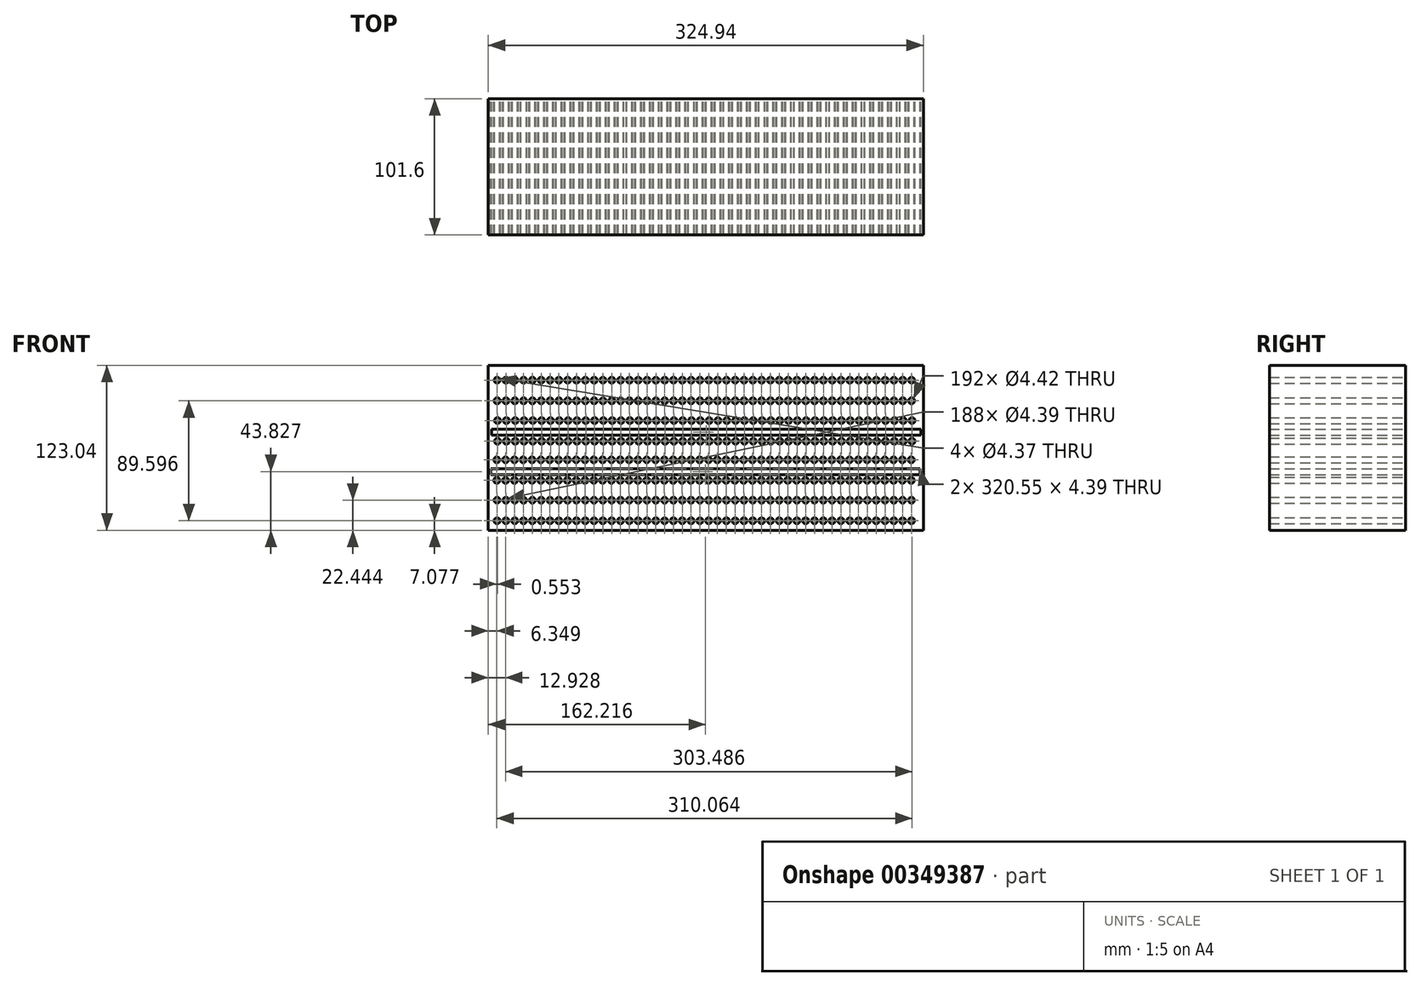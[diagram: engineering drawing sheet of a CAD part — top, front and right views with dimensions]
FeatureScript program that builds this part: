
annotation { "Feature Type Name" : "Feature", "Feature Type Description" : "" }
export const myFeature = defineFeature(function(context is Context, id is Id, definition is map)
    precondition{}
    {
        {
            var Q0;
            Q0=qCreatedBy(makeId("Front.planeOp"),FACE);
            var sketch = newSketch(context, id + "F0", { "sketchPlane" : qUnion([Q0])});
            skLineSegment(sketch, "E0.bottom", {"start": v(-162.47, -61.52) * mm, "end": v(162.47, -61.52) * mm});
            skLineSegment(sketch, "E0.top", {"start": v(-162.47, 61.52) * mm, "end": v(162.47, 61.52) * mm});
            skLineSegment(sketch, "E0.left", {"start": v(-162.47, -61.52) * mm, "end": v(-162.47, 61.52) * mm});
            skLineSegment(sketch, "E0.right", {"start": v(162.47, -61.52) * mm, "end": v(162.47, 61.52) * mm});
            skPoint(sketch, "E0.middle", {"position": v(0, 0) * mm});
            skLineSegment(sketch, "E1.left", {"start": v(-162.47, 61.52) * mm, "end": v(-162.47, 59.3) * mm});
            skLineSegment(sketch, "E1.right", {"start": v(162.47, 61.52) * mm, "end": v(162.47, 59.3) * mm});
            skLineSegment(sketch, "E2.top", {"start": v(-162.47, -61.52) * mm, "end": v(-160.27, -61.52) * mm});
            skLineSegment(sketch, "E2.left", {"start": v(-162.47, 59.3) * mm, "end": v(-162.47, -61.52) * mm});
            skLineSegment(sketch, "E3.top", {"start": v(162.47, -61.52) * mm, "end": v(160.27, -61.52) * mm});
            skLineSegment(sketch, "E3.left", {"start": v(162.47, 59.3) * mm, "end": v(162.47, -61.52) * mm});
            skLineSegment(sketch, "E4.bottom", {"start": v(-160.27, -61.52) * mm, "end": v(160.27, -61.52) * mm});
            skLineSegment(sketch, "E5.bottom", {"start": v(-160.27, 59.3) * mm, "end": v(160.27, 59.3) * mm});
            skLineSegment(sketch, "E5.top", {"start": v(-160.27, 54.91) * mm, "end": v(160.27, 54.91) * mm});
            skLineSegment(sketch, "E5.left", {"start": v(-160.27, 59.3) * mm, "end": v(-160.27, 54.91) * mm});
            skLineSegment(sketch, "E5.right", {"start": v(160.27, 59.3) * mm, "end": v(160.27, 54.91) * mm});
            skLineSegment(sketch, "E6.bottom", {"start": v(-160.27, 54.91) * mm, "end": v(-158.08, 54.91) * mm});
            skLineSegment(sketch, "E7.bottom", {"start": v(160.27, 54.91) * mm, "end": v(158.08, 54.91) * mm});
            skCircle(sketch, "E8", {"center": v(-155.87, 50.52) * mm, "radius": 2.18 * mm});
            skCircle(sketch, "E9", {"center": v(-149.29, 50.52) * mm, "radius": 2.2 * mm});
            skCircle(sketch, "E10", {"center": v(-142.68, 50.52) * mm, "radius": 2.2 * mm});
            skCircle(sketch, "E11", {"center": v(-136.1, 50.52) * mm, "radius": 2.2 * mm});
            skCircle(sketch, "E12", {"center": v(-129.51, 50.52) * mm, "radius": 2.2 * mm});
            skCircle(sketch, "E13", {"center": v(-122.94, 50.52) * mm, "radius": 2.2 * mm});
            skCircle(sketch, "E14", {"center": v(-116.34, 50.52) * mm, "radius": 2.2 * mm});
            skCircle(sketch, "E15", {"center": v(-109.77, 50.52) * mm, "radius": 2.2 * mm});
            skCircle(sketch, "E16", {"center": v(-103.17, 50.52) * mm, "radius": 2.2 * mm});
            skCircle(sketch, "E17", {"center": v(-96.6, 50.52) * mm, "radius": 2.2 * mm});
            skCircle(sketch, "E18", {"center": v(-90, 50.52) * mm, "radius": 2.2 * mm});
            skCircle(sketch, "E19", {"center": v(-83.43, 50.52) * mm, "radius": 2.2 * mm});
            skCircle(sketch, "E20", {"center": v(-76.84, 50.52) * mm, "radius": 2.2 * mm});
            skCircle(sketch, "E21", {"center": v(-70.26, 50.52) * mm, "radius": 2.2 * mm});
            skCircle(sketch, "E22", {"center": v(-63.67, 50.52) * mm, "radius": 2.2 * mm});
            skCircle(sketch, "E23", {"center": v(-57.09, 50.52) * mm, "radius": 2.2 * mm});
            skCircle(sketch, "E24", {"center": v(-50.5, 50.52) * mm, "radius": 2.2 * mm});
            skCircle(sketch, "E25", {"center": v(-43.92, 50.52) * mm, "radius": 2.2 * mm});
            skCircle(sketch, "E26", {"center": v(-37.33, 50.52) * mm, "radius": 2.2 * mm});
            skCircle(sketch, "E27", {"center": v(-30.75, 50.52) * mm, "radius": 2.2 * mm});
            skCircle(sketch, "E28", {"center": v(-24.16, 50.52) * mm, "radius": 2.2 * mm});
            skCircle(sketch, "E29", {"center": v(-17.58, 50.52) * mm, "radius": 2.2 * mm});
            skCircle(sketch, "E30", {"center": v(-10.99, 50.52) * mm, "radius": 2.2 * mm});
            skCircle(sketch, "E31", {"center": v(-4.4, 50.52) * mm, "radius": 2.2 * mm});
            skCircle(sketch, "E32", {"center": v(2.18, 50.52) * mm, "radius": 2.2 * mm});
            skCircle(sketch, "E33", {"center": v(8.76, 50.52) * mm, "radius": 2.2 * mm});
            skCircle(sketch, "E34", {"center": v(15.35, 50.52) * mm, "radius": 2.2 * mm});
            skCircle(sketch, "E35", {"center": v(21.93, 50.52) * mm, "radius": 2.2 * mm});
            skCircle(sketch, "E36", {"center": v(28.52, 50.52) * mm, "radius": 2.2 * mm});
            skCircle(sketch, "E37", {"center": v(35.1, 50.52) * mm, "radius": 2.2 * mm});
            skCircle(sketch, "E38", {"center": v(41.7, 50.52) * mm, "radius": 2.2 * mm});
            skCircle(sketch, "E39", {"center": v(48.27, 50.52) * mm, "radius": 2.2 * mm});
            skCircle(sketch, "E40", {"center": v(54.86, 50.52) * mm, "radius": 2.2 * mm});
            skCircle(sketch, "E41", {"center": v(61.44, 50.52) * mm, "radius": 2.2 * mm});
            skCircle(sketch, "E42", {"center": v(68.03, 50.52) * mm, "radius": 2.2 * mm});
            skCircle(sketch, "E43", {"center": v(74.61, 50.52) * mm, "radius": 2.2 * mm});
            skCircle(sketch, "E44", {"center": v(81.2, 50.52) * mm, "radius": 2.2 * mm});
            skCircle(sketch, "E45", {"center": v(87.78, 50.52) * mm, "radius": 2.2 * mm});
            skCircle(sketch, "E46", {"center": v(94.37, 50.52) * mm, "radius": 2.2 * mm});
            skCircle(sketch, "E47", {"center": v(100.95, 50.52) * mm, "radius": 2.2 * mm});
            skCircle(sketch, "E48", {"center": v(107.54, 50.52) * mm, "radius": 2.2 * mm});
            skCircle(sketch, "E49", {"center": v(114.12, 50.52) * mm, "radius": 2.2 * mm});
            skCircle(sketch, "E50", {"center": v(120.71, 50.52) * mm, "radius": 2.2 * mm});
            skCircle(sketch, "E51", {"center": v(127.3, 50.52) * mm, "radius": 2.2 * mm});
            skCircle(sketch, "E52", {"center": v(133.9, 50.52) * mm, "radius": 2.2 * mm});
            skCircle(sketch, "E53", {"center": v(140.47, 50.52) * mm, "radius": 2.2 * mm});
            skCircle(sketch, "E54", {"center": v(147.07, 50.52) * mm, "radius": 2.2 * mm});
            skCircle(sketch, "E55", {"center": v(153.64, 50.52) * mm, "radius": 2.2 * mm});
            skLineSegment(sketch, "E56", {"start": v(-155.87, 43.94) * mm, "end": v(-158.08, 43.94) * mm});
            skLineSegment(sketch, "E57", {"start": v(-158.08, 43.94) * mm, "end": v(-160.27, 43.94) * mm});
            skLineSegment(sketch, "E58.bottom", {"start": v(-160.27, 43.94) * mm, "end": v(160.27, 43.94) * mm});
            skLineSegment(sketch, "E58.top", {"start": v(-160.27, 39.55) * mm, "end": v(160.27, 39.55) * mm});
            skLineSegment(sketch, "E58.left", {"start": v(-160.27, 43.94) * mm, "end": v(-160.27, 39.55) * mm});
            skLineSegment(sketch, "E58.right", {"start": v(160.27, 43.94) * mm, "end": v(160.27, 39.55) * mm});
            skCircle(sketch, "E59", {"center": v(-155.87, 35.15) * mm, "radius": 2.2 * mm});
            skCircle(sketch, "E60", {"center": v(-149.29, 35.15) * mm, "radius": 2.2 * mm});
            skCircle(sketch, "E61", {"center": v(-142.68, 35.15) * mm, "radius": 2.2 * mm});
            skCircle(sketch, "E62", {"center": v(-136.1, 35.15) * mm, "radius": 2.2 * mm});
            skCircle(sketch, "E63", {"center": v(-129.51, 35.15) * mm, "radius": 2.2 * mm});
            skCircle(sketch, "E64", {"center": v(-122.94, 35.15) * mm, "radius": 2.2 * mm});
            skCircle(sketch, "E65", {"center": v(-116.34, 35.15) * mm, "radius": 2.2 * mm});
            skCircle(sketch, "E66", {"center": v(-109.77, 35.15) * mm, "radius": 2.2 * mm});
            skCircle(sketch, "E67", {"center": v(-103.17, 35.15) * mm, "radius": 2.2 * mm});
            skCircle(sketch, "E68", {"center": v(-96.6, 35.15) * mm, "radius": 2.2 * mm});
            skCircle(sketch, "E69", {"center": v(-90, 35.15) * mm, "radius": 2.2 * mm});
            skCircle(sketch, "E70", {"center": v(-83.43, 35.15) * mm, "radius": 2.2 * mm});
            skCircle(sketch, "E71", {"center": v(-76.84, 35.15) * mm, "radius": 2.2 * mm});
            skCircle(sketch, "E72", {"center": v(-70.26, 35.15) * mm, "radius": 2.2 * mm});
            skCircle(sketch, "E73", {"center": v(-63.67, 35.15) * mm, "radius": 2.2 * mm});
            skCircle(sketch, "E74", {"center": v(-57.09, 35.15) * mm, "radius": 2.2 * mm});
            skCircle(sketch, "E75", {"center": v(-50.5, 35.15) * mm, "radius": 2.2 * mm});
            skCircle(sketch, "E76", {"center": v(-43.92, 35.15) * mm, "radius": 2.2 * mm});
            skCircle(sketch, "E77", {"center": v(-37.33, 35.15) * mm, "radius": 2.2 * mm});
            skCircle(sketch, "E78", {"center": v(-30.75, 35.15) * mm, "radius": 2.2 * mm});
            skCircle(sketch, "E79", {"center": v(-24.16, 35.15) * mm, "radius": 2.2 * mm});
            skCircle(sketch, "E80", {"center": v(-17.58, 35.15) * mm, "radius": 2.2 * mm});
            skCircle(sketch, "E81", {"center": v(-10.99, 35.15) * mm, "radius": 2.2 * mm});
            skCircle(sketch, "E82", {"center": v(-4.4, 35.15) * mm, "radius": 2.2 * mm});
            skCircle(sketch, "E83", {"center": v(2.18, 35.15) * mm, "radius": 2.2 * mm});
            skCircle(sketch, "E84", {"center": v(8.76, 35.15) * mm, "radius": 2.2 * mm});
            skCircle(sketch, "E85", {"center": v(15.35, 35.15) * mm, "radius": 2.2 * mm});
            skCircle(sketch, "E86", {"center": v(21.93, 35.15) * mm, "radius": 2.2 * mm});
            skCircle(sketch, "E87", {"center": v(28.52, 35.15) * mm, "radius": 2.2 * mm});
            skCircle(sketch, "E88", {"center": v(35.1, 35.15) * mm, "radius": 2.2 * mm});
            skCircle(sketch, "E89", {"center": v(41.7, 35.15) * mm, "radius": 2.2 * mm});
            skCircle(sketch, "E90", {"center": v(48.27, 35.15) * mm, "radius": 2.2 * mm});
            skCircle(sketch, "E91", {"center": v(54.86, 35.15) * mm, "radius": 2.2 * mm});
            skCircle(sketch, "E92", {"center": v(61.44, 35.15) * mm, "radius": 2.2 * mm});
            skCircle(sketch, "E93", {"center": v(68.03, 35.15) * mm, "radius": 2.2 * mm});
            skCircle(sketch, "E94", {"center": v(74.61, 35.15) * mm, "radius": 2.2 * mm});
            skCircle(sketch, "E95", {"center": v(81.2, 35.15) * mm, "radius": 2.2 * mm});
            skCircle(sketch, "E96", {"center": v(87.78, 35.15) * mm, "radius": 2.2 * mm});
            skCircle(sketch, "E97", {"center": v(94.37, 35.15) * mm, "radius": 2.2 * mm});
            skCircle(sketch, "E98", {"center": v(100.95, 35.15) * mm, "radius": 2.2 * mm});
            skCircle(sketch, "E99", {"center": v(107.54, 35.15) * mm, "radius": 2.2 * mm});
            skCircle(sketch, "E100", {"center": v(114.12, 35.15) * mm, "radius": 2.2 * mm});
            skCircle(sketch, "E101", {"center": v(120.71, 35.15) * mm, "radius": 2.2 * mm});
            skCircle(sketch, "E102", {"center": v(127.3, 35.15) * mm, "radius": 2.2 * mm});
            skCircle(sketch, "E103", {"center": v(133.9, 35.15) * mm, "radius": 2.2 * mm});
            skCircle(sketch, "E104", {"center": v(140.47, 35.15) * mm, "radius": 2.2 * mm});
            skCircle(sketch, "E105", {"center": v(147.07, 35.15) * mm, "radius": 2.2 * mm});
            skCircle(sketch, "E106", {"center": v(153.64, 35.15) * mm, "radius": 2.2 * mm});
            skLineSegment(sketch, "E107.bottom", {"start": v(-159.97, 29.14) * mm, "end": v(160.57, 29.14) * mm});
            skLineSegment(sketch, "E107.top", {"start": v(-159.97, 24.75) * mm, "end": v(160.57, 24.75) * mm});
            skLineSegment(sketch, "E108.bottom", {"start": v(-159.97, 24.75) * mm, "end": v(-157.78, 24.75) * mm});
            skLineSegment(sketch, "E109.bottom", {"start": v(160.57, 24.75) * mm, "end": v(158.38, 24.75) * mm});
            skCircle(sketch, "E110", {"center": v(-155.57, 20.35) * mm, "radius": 2.18 * mm});
            skCircle(sketch, "E111", {"center": v(-148.99, 20.35) * mm, "radius": 2.2 * mm});
            skCircle(sketch, "E112", {"center": v(-142.39, 20.35) * mm, "radius": 2.2 * mm});
            skCircle(sketch, "E113", {"center": v(-135.8, 20.35) * mm, "radius": 2.2 * mm});
            skCircle(sketch, "E114", {"center": v(-129.22, 20.35) * mm, "radius": 2.2 * mm});
            skCircle(sketch, "E115", {"center": v(-122.64, 20.35) * mm, "radius": 2.2 * mm});
            skCircle(sketch, "E116", {"center": v(-116.05, 20.35) * mm, "radius": 2.2 * mm});
            skCircle(sketch, "E117", {"center": v(-109.47, 20.35) * mm, "radius": 2.2 * mm});
            skCircle(sketch, "E118", {"center": v(-102.88, 20.35) * mm, "radius": 2.2 * mm});
            skCircle(sketch, "E119", {"center": v(-96.3, 20.35) * mm, "radius": 2.2 * mm});
            skCircle(sketch, "E120", {"center": v(-89.7, 20.35) * mm, "radius": 2.2 * mm});
            skCircle(sketch, "E121", {"center": v(-83.13, 20.35) * mm, "radius": 2.2 * mm});
            skCircle(sketch, "E122", {"center": v(-76.54, 20.35) * mm, "radius": 2.2 * mm});
            skCircle(sketch, "E123", {"center": v(-69.96, 20.35) * mm, "radius": 2.2 * mm});
            skCircle(sketch, "E124", {"center": v(-63.37, 20.35) * mm, "radius": 2.2 * mm});
            skCircle(sketch, "E125", {"center": v(-56.79, 20.35) * mm, "radius": 2.2 * mm});
            skCircle(sketch, "E126", {"center": v(-50.2, 20.35) * mm, "radius": 2.2 * mm});
            skCircle(sketch, "E127", {"center": v(-43.62, 20.35) * mm, "radius": 2.2 * mm});
            skCircle(sketch, "E128", {"center": v(-37.03, 20.35) * mm, "radius": 2.2 * mm});
            skCircle(sketch, "E129", {"center": v(-30.45, 20.35) * mm, "radius": 2.2 * mm});
            skCircle(sketch, "E130", {"center": v(-23.86, 20.35) * mm, "radius": 2.2 * mm});
            skCircle(sketch, "E131", {"center": v(-17.28, 20.35) * mm, "radius": 2.2 * mm});
            skCircle(sketch, "E132", {"center": v(-10.69, 20.35) * mm, "radius": 2.2 * mm});
            skCircle(sketch, "E133", {"center": v(-4.1, 20.35) * mm, "radius": 2.2 * mm});
            skCircle(sketch, "E134", {"center": v(2.48, 20.35) * mm, "radius": 2.2 * mm});
            skCircle(sketch, "E135", {"center": v(9.06, 20.35) * mm, "radius": 2.2 * mm});
            skCircle(sketch, "E136", {"center": v(15.65, 20.35) * mm, "radius": 2.2 * mm});
            skCircle(sketch, "E137", {"center": v(22.23, 20.35) * mm, "radius": 2.2 * mm});
            skCircle(sketch, "E138", {"center": v(28.82, 20.35) * mm, "radius": 2.2 * mm});
            skCircle(sketch, "E139", {"center": v(35.4, 20.35) * mm, "radius": 2.2 * mm});
            skCircle(sketch, "E140", {"center": v(42, 20.35) * mm, "radius": 2.2 * mm});
            skCircle(sketch, "E141", {"center": v(48.57, 20.35) * mm, "radius": 2.2 * mm});
            skCircle(sketch, "E142", {"center": v(55.16, 20.35) * mm, "radius": 2.2 * mm});
            skCircle(sketch, "E143", {"center": v(61.74, 20.35) * mm, "radius": 2.2 * mm});
            skCircle(sketch, "E144", {"center": v(68.33, 20.35) * mm, "radius": 2.2 * mm});
            skCircle(sketch, "E145", {"center": v(74.91, 20.35) * mm, "radius": 2.2 * mm});
            skCircle(sketch, "E146", {"center": v(81.5, 20.35) * mm, "radius": 2.2 * mm});
            skCircle(sketch, "E147", {"center": v(88.08, 20.35) * mm, "radius": 2.2 * mm});
            skCircle(sketch, "E148", {"center": v(94.67, 20.35) * mm, "radius": 2.2 * mm});
            skCircle(sketch, "E149", {"center": v(101.25, 20.35) * mm, "radius": 2.2 * mm});
            skCircle(sketch, "E150", {"center": v(107.84, 20.35) * mm, "radius": 2.2 * mm});
            skCircle(sketch, "E151", {"center": v(114.42, 20.35) * mm, "radius": 2.2 * mm});
            skCircle(sketch, "E152", {"center": v(121.01, 20.35) * mm, "radius": 2.2 * mm});
            skCircle(sketch, "E153", {"center": v(127.6, 20.35) * mm, "radius": 2.2 * mm});
            skCircle(sketch, "E154", {"center": v(134.2, 20.35) * mm, "radius": 2.2 * mm});
            skCircle(sketch, "E155", {"center": v(140.77, 20.35) * mm, "radius": 2.2 * mm});
            skCircle(sketch, "E156", {"center": v(147.37, 20.35) * mm, "radius": 2.2 * mm});
            skCircle(sketch, "E157", {"center": v(153.94, 20.35) * mm, "radius": 2.2 * mm});
            skLineSegment(sketch, "E158", {"start": v(-155.57, 13.77) * mm, "end": v(-157.78, 13.77) * mm});
            skLineSegment(sketch, "E159", {"start": v(-157.78, 13.77) * mm, "end": v(-159.97, 13.77) * mm});
            skLineSegment(sketch, "E160.bottom", {"start": v(-159.97, 13.77) * mm, "end": v(160.57, 13.77) * mm});
            skLineSegment(sketch, "E160.top", {"start": v(-159.97, 9.38) * mm, "end": v(160.57, 9.38) * mm});
            skCircle(sketch, "E161", {"center": v(-155.57, 4.99) * mm, "radius": 2.2 * mm});
            skCircle(sketch, "E162", {"center": v(-148.99, 4.99) * mm, "radius": 2.2 * mm});
            skCircle(sketch, "E163", {"center": v(-142.39, 4.99) * mm, "radius": 2.2 * mm});
            skCircle(sketch, "E164", {"center": v(-135.8, 4.99) * mm, "radius": 2.2 * mm});
            skCircle(sketch, "E165", {"center": v(-129.22, 4.99) * mm, "radius": 2.2 * mm});
            skCircle(sketch, "E166", {"center": v(-122.64, 4.99) * mm, "radius": 2.2 * mm});
            skCircle(sketch, "E167", {"center": v(-116.05, 4.99) * mm, "radius": 2.2 * mm});
            skCircle(sketch, "E168", {"center": v(-109.47, 4.99) * mm, "radius": 2.2 * mm});
            skCircle(sketch, "E169", {"center": v(-102.88, 4.99) * mm, "radius": 2.2 * mm});
            skCircle(sketch, "E170", {"center": v(-96.3, 4.99) * mm, "radius": 2.2 * mm});
            skCircle(sketch, "E171", {"center": v(-89.7, 4.99) * mm, "radius": 2.2 * mm});
            skCircle(sketch, "E172", {"center": v(-83.13, 4.99) * mm, "radius": 2.2 * mm});
            skCircle(sketch, "E173", {"center": v(-76.54, 4.99) * mm, "radius": 2.2 * mm});
            skCircle(sketch, "E174", {"center": v(-69.96, 4.99) * mm, "radius": 2.2 * mm});
            skCircle(sketch, "E175", {"center": v(-63.37, 4.99) * mm, "radius": 2.2 * mm});
            skCircle(sketch, "E176", {"center": v(-56.79, 4.99) * mm, "radius": 2.2 * mm});
            skCircle(sketch, "E177", {"center": v(-50.2, 4.99) * mm, "radius": 2.2 * mm});
            skCircle(sketch, "E178", {"center": v(-43.62, 4.99) * mm, "radius": 2.2 * mm});
            skCircle(sketch, "E179", {"center": v(-37.03, 4.99) * mm, "radius": 2.2 * mm});
            skCircle(sketch, "E180", {"center": v(-30.45, 4.99) * mm, "radius": 2.2 * mm});
            skCircle(sketch, "E181", {"center": v(-23.86, 4.99) * mm, "radius": 2.2 * mm});
            skCircle(sketch, "E182", {"center": v(-17.28, 4.99) * mm, "radius": 2.2 * mm});
            skCircle(sketch, "E183", {"center": v(-10.69, 4.99) * mm, "radius": 2.2 * mm});
            skCircle(sketch, "E184", {"center": v(-4.1, 4.99) * mm, "radius": 2.2 * mm});
            skCircle(sketch, "E185", {"center": v(2.48, 4.99) * mm, "radius": 2.2 * mm});
            skCircle(sketch, "E186", {"center": v(9.06, 4.99) * mm, "radius": 2.2 * mm});
            skCircle(sketch, "E187", {"center": v(15.65, 4.99) * mm, "radius": 2.2 * mm});
            skCircle(sketch, "E188", {"center": v(22.23, 4.99) * mm, "radius": 2.2 * mm});
            skCircle(sketch, "E189", {"center": v(28.82, 4.99) * mm, "radius": 2.2 * mm});
            skCircle(sketch, "E190", {"center": v(35.4, 4.99) * mm, "radius": 2.2 * mm});
            skCircle(sketch, "E191", {"center": v(42, 4.99) * mm, "radius": 2.2 * mm});
            skCircle(sketch, "E192", {"center": v(48.57, 4.99) * mm, "radius": 2.2 * mm});
            skCircle(sketch, "E193", {"center": v(55.16, 4.99) * mm, "radius": 2.2 * mm});
            skCircle(sketch, "E194", {"center": v(61.74, 4.99) * mm, "radius": 2.2 * mm});
            skCircle(sketch, "E195", {"center": v(68.33, 4.99) * mm, "radius": 2.2 * mm});
            skCircle(sketch, "E196", {"center": v(74.91, 4.99) * mm, "radius": 2.2 * mm});
            skCircle(sketch, "E197", {"center": v(81.5, 4.99) * mm, "radius": 2.2 * mm});
            skCircle(sketch, "E198", {"center": v(88.08, 4.99) * mm, "radius": 2.2 * mm});
            skCircle(sketch, "E199", {"center": v(94.67, 4.99) * mm, "radius": 2.2 * mm});
            skCircle(sketch, "E200", {"center": v(101.25, 4.99) * mm, "radius": 2.2 * mm});
            skCircle(sketch, "E201", {"center": v(107.84, 4.99) * mm, "radius": 2.2 * mm});
            skCircle(sketch, "E202", {"center": v(114.42, 4.99) * mm, "radius": 2.2 * mm});
            skCircle(sketch, "E203", {"center": v(121.01, 4.99) * mm, "radius": 2.2 * mm});
            skCircle(sketch, "E204", {"center": v(127.6, 4.99) * mm, "radius": 2.2 * mm});
            skCircle(sketch, "E205", {"center": v(134.2, 4.99) * mm, "radius": 2.2 * mm});
            skCircle(sketch, "E206", {"center": v(140.77, 4.99) * mm, "radius": 2.2 * mm});
            skCircle(sketch, "E207", {"center": v(147.37, 4.99) * mm, "radius": 2.2 * mm});
            skCircle(sketch, "E208", {"center": v(153.94, 4.99) * mm, "radius": 2.2 * mm});
            skLineSegment(sketch, "E209.bottom", {"start": v(-160.53, -0.13) * mm, "end": v(160.02, -0.13) * mm});
            skLineSegment(sketch, "E209.top", {"start": v(-160.53, -4.52) * mm, "end": v(160.02, -4.52) * mm});
            skLineSegment(sketch, "E210.bottom", {"start": v(-160.53, -4.52) * mm, "end": v(-158.33, -4.52) * mm});
            skLineSegment(sketch, "E211.bottom", {"start": v(160.02, -4.52) * mm, "end": v(157.82, -4.52) * mm});
            skCircle(sketch, "E212", {"center": v(-156.12, -8.92) * mm, "radius": 2.18 * mm});
            skCircle(sketch, "E213", {"center": v(-149.54, -8.92) * mm, "radius": 2.2 * mm});
            skCircle(sketch, "E214", {"center": v(-142.94, -8.92) * mm, "radius": 2.2 * mm});
            skCircle(sketch, "E215", {"center": v(-136.36, -8.92) * mm, "radius": 2.2 * mm});
            skCircle(sketch, "E216", {"center": v(-129.77, -8.92) * mm, "radius": 2.2 * mm});
            skCircle(sketch, "E217", {"center": v(-123.19, -8.92) * mm, "radius": 2.2 * mm});
            skCircle(sketch, "E218", {"center": v(-116.6, -8.92) * mm, "radius": 2.2 * mm});
            skCircle(sketch, "E219", {"center": v(-110.02, -8.92) * mm, "radius": 2.2 * mm});
            skCircle(sketch, "E220", {"center": v(-103.43, -8.92) * mm, "radius": 2.2 * mm});
            skCircle(sketch, "E221", {"center": v(-96.85, -8.92) * mm, "radius": 2.2 * mm});
            skCircle(sketch, "E222", {"center": v(-90.26, -8.92) * mm, "radius": 2.2 * mm});
            skCircle(sketch, "E223", {"center": v(-83.68, -8.92) * mm, "radius": 2.2 * mm});
            skCircle(sketch, "E224", {"center": v(-77.09, -8.92) * mm, "radius": 2.2 * mm});
            skCircle(sketch, "E225", {"center": v(-70.5, -8.92) * mm, "radius": 2.2 * mm});
            skCircle(sketch, "E226", {"center": v(-63.92, -8.92) * mm, "radius": 2.2 * mm});
            skCircle(sketch, "E227", {"center": v(-57.34, -8.92) * mm, "radius": 2.2 * mm});
            skCircle(sketch, "E228", {"center": v(-50.75, -8.92) * mm, "radius": 2.2 * mm});
            skCircle(sketch, "E229", {"center": v(-44.17, -8.92) * mm, "radius": 2.2 * mm});
            skCircle(sketch, "E230", {"center": v(-37.58, -8.92) * mm, "radius": 2.2 * mm});
            skCircle(sketch, "E231", {"center": v(-31, -8.92) * mm, "radius": 2.2 * mm});
            skCircle(sketch, "E232", {"center": v(-24.4, -8.92) * mm, "radius": 2.2 * mm});
            skCircle(sketch, "E233", {"center": v(-17.83, -8.92) * mm, "radius": 2.2 * mm});
            skCircle(sketch, "E234", {"center": v(-11.24, -8.92) * mm, "radius": 2.2 * mm});
            skCircle(sketch, "E235", {"center": v(-4.66, -8.92) * mm, "radius": 2.2 * mm});
            skCircle(sketch, "E236", {"center": v(1.93, -8.92) * mm, "radius": 2.2 * mm});
            skCircle(sketch, "E237", {"center": v(8.5, -8.92) * mm, "radius": 2.2 * mm});
            skCircle(sketch, "E238", {"center": v(15.1, -8.92) * mm, "radius": 2.2 * mm});
            skCircle(sketch, "E239", {"center": v(21.68, -8.92) * mm, "radius": 2.2 * mm});
            skCircle(sketch, "E240", {"center": v(28.27, -8.92) * mm, "radius": 2.2 * mm});
            skCircle(sketch, "E241", {"center": v(34.85, -8.92) * mm, "radius": 2.2 * mm});
            skCircle(sketch, "E242", {"center": v(41.44, -8.92) * mm, "radius": 2.2 * mm});
            skCircle(sketch, "E243", {"center": v(48.02, -8.92) * mm, "radius": 2.2 * mm});
            skCircle(sketch, "E244", {"center": v(54.61, -8.92) * mm, "radius": 2.2 * mm});
            skCircle(sketch, "E245", {"center": v(61.19, -8.92) * mm, "radius": 2.2 * mm});
            skCircle(sketch, "E246", {"center": v(67.78, -8.92) * mm, "radius": 2.2 * mm});
            skCircle(sketch, "E247", {"center": v(74.36, -8.92) * mm, "radius": 2.2 * mm});
            skCircle(sketch, "E248", {"center": v(80.95, -8.92) * mm, "radius": 2.2 * mm});
            skCircle(sketch, "E249", {"center": v(87.53, -8.92) * mm, "radius": 2.2 * mm});
            skCircle(sketch, "E250", {"center": v(94.12, -8.92) * mm, "radius": 2.2 * mm});
            skCircle(sketch, "E251", {"center": v(100.7, -8.92) * mm, "radius": 2.2 * mm});
            skCircle(sketch, "E252", {"center": v(107.3, -8.92) * mm, "radius": 2.2 * mm});
            skCircle(sketch, "E253", {"center": v(113.87, -8.92) * mm, "radius": 2.2 * mm});
            skCircle(sketch, "E254", {"center": v(120.46, -8.92) * mm, "radius": 2.2 * mm});
            skCircle(sketch, "E255", {"center": v(127.05, -8.92) * mm, "radius": 2.2 * mm});
            skCircle(sketch, "E256", {"center": v(133.64, -8.92) * mm, "radius": 2.2 * mm});
            skCircle(sketch, "E257", {"center": v(140.22, -8.92) * mm, "radius": 2.2 * mm});
            skCircle(sketch, "E258", {"center": v(146.81, -8.92) * mm, "radius": 2.2 * mm});
            skCircle(sketch, "E259", {"center": v(153.4, -8.92) * mm, "radius": 2.2 * mm});
            skLineSegment(sketch, "E260", {"start": v(-156.12, -15.5) * mm, "end": v(-158.33, -15.5) * mm});
            skLineSegment(sketch, "E261", {"start": v(-158.33, -15.5) * mm, "end": v(-160.53, -15.5) * mm});
            skLineSegment(sketch, "E262.bottom", {"start": v(-160.53, -15.5) * mm, "end": v(160.02, -15.5) * mm});
            skLineSegment(sketch, "E262.top", {"start": v(-160.53, -19.9) * mm, "end": v(160.02, -19.9) * mm});
            skCircle(sketch, "E263", {"center": v(-156.12, -24.28) * mm, "radius": 2.2 * mm});
            skCircle(sketch, "E264", {"center": v(-149.54, -24.28) * mm, "radius": 2.2 * mm});
            skCircle(sketch, "E265", {"center": v(-142.94, -24.28) * mm, "radius": 2.2 * mm});
            skCircle(sketch, "E266", {"center": v(-136.36, -24.28) * mm, "radius": 2.2 * mm});
            skCircle(sketch, "E267", {"center": v(-129.77, -24.28) * mm, "radius": 2.2 * mm});
            skCircle(sketch, "E268", {"center": v(-123.19, -24.28) * mm, "radius": 2.2 * mm});
            skCircle(sketch, "E269", {"center": v(-116.6, -24.28) * mm, "radius": 2.2 * mm});
            skCircle(sketch, "E270", {"center": v(-110.02, -24.28) * mm, "radius": 2.2 * mm});
            skCircle(sketch, "E271", {"center": v(-103.43, -24.28) * mm, "radius": 2.2 * mm});
            skCircle(sketch, "E272", {"center": v(-96.85, -24.28) * mm, "radius": 2.2 * mm});
            skCircle(sketch, "E273", {"center": v(-90.26, -24.28) * mm, "radius": 2.2 * mm});
            skCircle(sketch, "E274", {"center": v(-83.68, -24.28) * mm, "radius": 2.2 * mm});
            skCircle(sketch, "E275", {"center": v(-77.09, -24.28) * mm, "radius": 2.2 * mm});
            skCircle(sketch, "E276", {"center": v(-70.5, -24.28) * mm, "radius": 2.2 * mm});
            skCircle(sketch, "E277", {"center": v(-63.92, -24.28) * mm, "radius": 2.2 * mm});
            skCircle(sketch, "E278", {"center": v(-57.34, -24.28) * mm, "radius": 2.2 * mm});
            skCircle(sketch, "E279", {"center": v(-50.75, -24.28) * mm, "radius": 2.2 * mm});
            skCircle(sketch, "E280", {"center": v(-44.17, -24.28) * mm, "radius": 2.2 * mm});
            skCircle(sketch, "E281", {"center": v(-37.58, -24.28) * mm, "radius": 2.2 * mm});
            skCircle(sketch, "E282", {"center": v(-31, -24.28) * mm, "radius": 2.2 * mm});
            skCircle(sketch, "E283", {"center": v(-24.4, -24.28) * mm, "radius": 2.2 * mm});
            skCircle(sketch, "E284", {"center": v(-17.83, -24.28) * mm, "radius": 2.2 * mm});
            skCircle(sketch, "E285", {"center": v(-11.24, -24.28) * mm, "radius": 2.2 * mm});
            skCircle(sketch, "E286", {"center": v(-4.66, -24.28) * mm, "radius": 2.2 * mm});
            skCircle(sketch, "E287", {"center": v(1.93, -24.28) * mm, "radius": 2.2 * mm});
            skCircle(sketch, "E288", {"center": v(8.5, -24.28) * mm, "radius": 2.2 * mm});
            skCircle(sketch, "E289", {"center": v(15.1, -24.28) * mm, "radius": 2.2 * mm});
            skCircle(sketch, "E290", {"center": v(21.68, -24.28) * mm, "radius": 2.2 * mm});
            skCircle(sketch, "E291", {"center": v(28.27, -24.28) * mm, "radius": 2.2 * mm});
            skCircle(sketch, "E292", {"center": v(34.85, -24.28) * mm, "radius": 2.2 * mm});
            skCircle(sketch, "E293", {"center": v(41.44, -24.28) * mm, "radius": 2.2 * mm});
            skCircle(sketch, "E294", {"center": v(48.02, -24.28) * mm, "radius": 2.2 * mm});
            skCircle(sketch, "E295", {"center": v(54.61, -24.28) * mm, "radius": 2.2 * mm});
            skCircle(sketch, "E296", {"center": v(61.19, -24.28) * mm, "radius": 2.2 * mm});
            skCircle(sketch, "E297", {"center": v(67.78, -24.28) * mm, "radius": 2.2 * mm});
            skCircle(sketch, "E298", {"center": v(74.36, -24.28) * mm, "radius": 2.2 * mm});
            skCircle(sketch, "E299", {"center": v(80.95, -24.28) * mm, "radius": 2.2 * mm});
            skCircle(sketch, "E300", {"center": v(87.53, -24.28) * mm, "radius": 2.2 * mm});
            skCircle(sketch, "E301", {"center": v(94.12, -24.28) * mm, "radius": 2.2 * mm});
            skCircle(sketch, "E302", {"center": v(100.7, -24.28) * mm, "radius": 2.2 * mm});
            skCircle(sketch, "E303", {"center": v(107.3, -24.28) * mm, "radius": 2.2 * mm});
            skCircle(sketch, "E304", {"center": v(113.87, -24.28) * mm, "radius": 2.2 * mm});
            skCircle(sketch, "E305", {"center": v(120.46, -24.28) * mm, "radius": 2.2 * mm});
            skCircle(sketch, "E306", {"center": v(127.05, -24.28) * mm, "radius": 2.2 * mm});
            skCircle(sketch, "E307", {"center": v(133.64, -24.28) * mm, "radius": 2.2 * mm});
            skCircle(sketch, "E308", {"center": v(140.22, -24.28) * mm, "radius": 2.2 * mm});
            skCircle(sketch, "E309", {"center": v(146.81, -24.28) * mm, "radius": 2.2 * mm});
            skCircle(sketch, "E310", {"center": v(153.4, -24.28) * mm, "radius": 2.2 * mm});
            skLineSegment(sketch, "E311.left", {"start": v(-162.53, -28.08) * mm, "end": v(-162.53, -30.29) * mm});
            skLineSegment(sketch, "E312.bottom", {"start": v(-160.33, -30.29) * mm, "end": v(160.21, -30.29) * mm});
            skLineSegment(sketch, "E312.top", {"start": v(-160.33, -34.68) * mm, "end": v(160.21, -34.68) * mm});
            skLineSegment(sketch, "E312.left", {"start": v(-160.33, -30.29) * mm, "end": v(-160.33, -34.68) * mm});
            skLineSegment(sketch, "E312.right", {"start": v(160.21, -30.29) * mm, "end": v(160.21, -34.68) * mm});
            skLineSegment(sketch, "E313.bottom", {"start": v(-160.33, -34.68) * mm, "end": v(-158.14, -34.68) * mm});
            skLineSegment(sketch, "E314.bottom", {"start": v(160.21, -34.68) * mm, "end": v(158.02, -34.68) * mm});
            skCircle(sketch, "E315", {"center": v(-155.93, -39.08) * mm, "radius": 2.18 * mm});
            skCircle(sketch, "E316", {"center": v(-149.35, -39.08) * mm, "radius": 2.2 * mm});
            skCircle(sketch, "E317", {"center": v(-142.75, -39.08) * mm, "radius": 2.2 * mm});
            skCircle(sketch, "E318", {"center": v(-136.17, -39.08) * mm, "radius": 2.2 * mm});
            skCircle(sketch, "E319", {"center": v(-129.58, -39.08) * mm, "radius": 2.2 * mm});
            skCircle(sketch, "E320", {"center": v(-123, -39.08) * mm, "radius": 2.2 * mm});
            skCircle(sketch, "E321", {"center": v(-116.4, -39.08) * mm, "radius": 2.2 * mm});
            skCircle(sketch, "E322", {"center": v(-109.83, -39.08) * mm, "radius": 2.2 * mm});
            skCircle(sketch, "E323", {"center": v(-103.24, -39.08) * mm, "radius": 2.2 * mm});
            skCircle(sketch, "E324", {"center": v(-96.66, -39.08) * mm, "radius": 2.2 * mm});
            skCircle(sketch, "E325", {"center": v(-90.07, -39.08) * mm, "radius": 2.2 * mm});
            skCircle(sketch, "E326", {"center": v(-83.49, -39.08) * mm, "radius": 2.2 * mm});
            skCircle(sketch, "E327", {"center": v(-76.9, -39.08) * mm, "radius": 2.2 * mm});
            skCircle(sketch, "E328", {"center": v(-70.32, -39.08) * mm, "radius": 2.2 * mm});
            skCircle(sketch, "E329", {"center": v(-63.73, -39.08) * mm, "radius": 2.2 * mm});
            skCircle(sketch, "E330", {"center": v(-57.15, -39.08) * mm, "radius": 2.2 * mm});
            skCircle(sketch, "E331", {"center": v(-50.56, -39.08) * mm, "radius": 2.2 * mm});
            skCircle(sketch, "E332", {"center": v(-43.98, -39.08) * mm, "radius": 2.2 * mm});
            skCircle(sketch, "E333", {"center": v(-37.39, -39.08) * mm, "radius": 2.2 * mm});
            skCircle(sketch, "E334", {"center": v(-30.8, -39.08) * mm, "radius": 2.2 * mm});
            skCircle(sketch, "E335", {"center": v(-24.22, -39.08) * mm, "radius": 2.2 * mm});
            skCircle(sketch, "E336", {"center": v(-17.64, -39.08) * mm, "radius": 2.2 * mm});
            skCircle(sketch, "E337", {"center": v(-11.05, -39.08) * mm, "radius": 2.2 * mm});
            skCircle(sketch, "E338", {"center": v(-4.47, -39.08) * mm, "radius": 2.2 * mm});
            skCircle(sketch, "E339", {"center": v(2.12, -39.08) * mm, "radius": 2.2 * mm});
            skCircle(sketch, "E340", {"center": v(8.7, -39.08) * mm, "radius": 2.2 * mm});
            skCircle(sketch, "E341", {"center": v(15.3, -39.08) * mm, "radius": 2.2 * mm});
            skCircle(sketch, "E342", {"center": v(21.87, -39.08) * mm, "radius": 2.2 * mm});
            skCircle(sketch, "E343", {"center": v(28.46, -39.08) * mm, "radius": 2.2 * mm});
            skCircle(sketch, "E344", {"center": v(35.04, -39.08) * mm, "radius": 2.2 * mm});
            skCircle(sketch, "E345", {"center": v(41.63, -39.08) * mm, "radius": 2.2 * mm});
            skCircle(sketch, "E346", {"center": v(48.21, -39.08) * mm, "radius": 2.2 * mm});
            skCircle(sketch, "E347", {"center": v(54.8, -39.08) * mm, "radius": 2.2 * mm});
            skCircle(sketch, "E348", {"center": v(61.38, -39.08) * mm, "radius": 2.2 * mm});
            skCircle(sketch, "E349", {"center": v(67.97, -39.08) * mm, "radius": 2.2 * mm});
            skCircle(sketch, "E350", {"center": v(74.55, -39.08) * mm, "radius": 2.2 * mm});
            skCircle(sketch, "E351", {"center": v(81.14, -39.08) * mm, "radius": 2.2 * mm});
            skCircle(sketch, "E352", {"center": v(87.72, -39.08) * mm, "radius": 2.2 * mm});
            skCircle(sketch, "E353", {"center": v(94.31, -39.08) * mm, "radius": 2.2 * mm});
            skCircle(sketch, "E354", {"center": v(100.9, -39.08) * mm, "radius": 2.2 * mm});
            skCircle(sketch, "E355", {"center": v(107.48, -39.08) * mm, "radius": 2.2 * mm});
            skCircle(sketch, "E356", {"center": v(114.06, -39.08) * mm, "radius": 2.2 * mm});
            skCircle(sketch, "E357", {"center": v(120.65, -39.08) * mm, "radius": 2.2 * mm});
            skCircle(sketch, "E358", {"center": v(127.24, -39.08) * mm, "radius": 2.2 * mm});
            skCircle(sketch, "E359", {"center": v(133.84, -39.08) * mm, "radius": 2.2 * mm});
            skCircle(sketch, "E360", {"center": v(140.41, -39.08) * mm, "radius": 2.2 * mm});
            skCircle(sketch, "E361", {"center": v(147, -39.08) * mm, "radius": 2.2 * mm});
            skCircle(sketch, "E362", {"center": v(153.58, -39.08) * mm, "radius": 2.2 * mm});
            skLineSegment(sketch, "E363", {"start": v(-155.93, -45.65) * mm, "end": v(-158.14, -45.65) * mm});
            skLineSegment(sketch, "E364", {"start": v(-158.14, -45.65) * mm, "end": v(-160.33, -45.65) * mm});
            skLineSegment(sketch, "E365.bottom", {"start": v(-160.33, -45.65) * mm, "end": v(160.21, -45.65) * mm});
            skLineSegment(sketch, "E365.top", {"start": v(-160.33, -50.05) * mm, "end": v(160.21, -50.05) * mm});
            skLineSegment(sketch, "E365.left", {"start": v(-160.33, -45.65) * mm, "end": v(-160.33, -50.05) * mm});
            skLineSegment(sketch, "E365.right", {"start": v(160.21, -45.65) * mm, "end": v(160.21, -50.05) * mm});
            skCircle(sketch, "E366", {"center": v(-155.93, -54.44) * mm, "radius": 2.2 * mm});
            skCircle(sketch, "E367", {"center": v(-149.35, -54.44) * mm, "radius": 2.2 * mm});
            skCircle(sketch, "E368", {"center": v(-142.75, -54.44) * mm, "radius": 2.2 * mm});
            skCircle(sketch, "E369", {"center": v(-136.17, -54.44) * mm, "radius": 2.2 * mm});
            skCircle(sketch, "E370", {"center": v(-129.58, -54.44) * mm, "radius": 2.2 * mm});
            skCircle(sketch, "E371", {"center": v(-123, -54.44) * mm, "radius": 2.2 * mm});
            skCircle(sketch, "E372", {"center": v(-116.4, -54.44) * mm, "radius": 2.2 * mm});
            skCircle(sketch, "E373", {"center": v(-109.83, -54.44) * mm, "radius": 2.2 * mm});
            skCircle(sketch, "E374", {"center": v(-103.24, -54.44) * mm, "radius": 2.2 * mm});
            skCircle(sketch, "E375", {"center": v(-96.66, -54.44) * mm, "radius": 2.2 * mm});
            skCircle(sketch, "E376", {"center": v(-90.07, -54.44) * mm, "radius": 2.2 * mm});
            skCircle(sketch, "E377", {"center": v(-83.49, -54.44) * mm, "radius": 2.2 * mm});
            skCircle(sketch, "E378", {"center": v(-76.9, -54.44) * mm, "radius": 2.2 * mm});
            skCircle(sketch, "E379", {"center": v(-70.32, -54.44) * mm, "radius": 2.2 * mm});
            skCircle(sketch, "E380", {"center": v(-63.73, -54.44) * mm, "radius": 2.2 * mm});
            skCircle(sketch, "E381", {"center": v(-57.15, -54.44) * mm, "radius": 2.2 * mm});
            skCircle(sketch, "E382", {"center": v(-50.56, -54.44) * mm, "radius": 2.2 * mm});
            skCircle(sketch, "E383", {"center": v(-43.98, -54.44) * mm, "radius": 2.2 * mm});
            skCircle(sketch, "E384", {"center": v(-37.39, -54.44) * mm, "radius": 2.2 * mm});
            skCircle(sketch, "E385", {"center": v(-30.8, -54.44) * mm, "radius": 2.2 * mm});
            skCircle(sketch, "E386", {"center": v(-24.22, -54.44) * mm, "radius": 2.2 * mm});
            skCircle(sketch, "E387", {"center": v(-17.64, -54.44) * mm, "radius": 2.2 * mm});
            skCircle(sketch, "E388", {"center": v(-11.05, -54.44) * mm, "radius": 2.2 * mm});
            skCircle(sketch, "E389", {"center": v(-4.47, -54.44) * mm, "radius": 2.2 * mm});
            skCircle(sketch, "E390", {"center": v(2.12, -54.44) * mm, "radius": 2.2 * mm});
            skCircle(sketch, "E391", {"center": v(8.7, -54.44) * mm, "radius": 2.2 * mm});
            skCircle(sketch, "E392", {"center": v(15.3, -54.44) * mm, "radius": 2.2 * mm});
            skCircle(sketch, "E393", {"center": v(21.87, -54.44) * mm, "radius": 2.2 * mm});
            skCircle(sketch, "E394", {"center": v(28.46, -54.44) * mm, "radius": 2.2 * mm});
            skCircle(sketch, "E395", {"center": v(35.04, -54.44) * mm, "radius": 2.2 * mm});
            skCircle(sketch, "E396", {"center": v(41.63, -54.44) * mm, "radius": 2.2 * mm});
            skCircle(sketch, "E397", {"center": v(48.21, -54.44) * mm, "radius": 2.2 * mm});
            skCircle(sketch, "E398", {"center": v(54.8, -54.44) * mm, "radius": 2.2 * mm});
            skCircle(sketch, "E399", {"center": v(61.38, -54.44) * mm, "radius": 2.2 * mm});
            skCircle(sketch, "E400", {"center": v(67.97, -54.44) * mm, "radius": 2.2 * mm});
            skCircle(sketch, "E401", {"center": v(74.55, -54.44) * mm, "radius": 2.2 * mm});
            skCircle(sketch, "E402", {"center": v(81.14, -54.44) * mm, "radius": 2.2 * mm});
            skCircle(sketch, "E403", {"center": v(87.72, -54.44) * mm, "radius": 2.2 * mm});
            skCircle(sketch, "E404", {"center": v(94.31, -54.44) * mm, "radius": 2.2 * mm});
            skCircle(sketch, "E405", {"center": v(100.9, -54.44) * mm, "radius": 2.2 * mm});
            skCircle(sketch, "E406", {"center": v(107.48, -54.44) * mm, "radius": 2.2 * mm});
            skCircle(sketch, "E407", {"center": v(114.06, -54.44) * mm, "radius": 2.2 * mm});
            skCircle(sketch, "E408", {"center": v(120.65, -54.44) * mm, "radius": 2.2 * mm});
            skCircle(sketch, "E409", {"center": v(127.24, -54.44) * mm, "radius": 2.2 * mm});
            skCircle(sketch, "E410", {"center": v(133.84, -54.44) * mm, "radius": 2.2 * mm});
            skCircle(sketch, "E411", {"center": v(140.41, -54.44) * mm, "radius": 2.2 * mm});
            skCircle(sketch, "E412", {"center": v(147, -54.44) * mm, "radius": 2.2 * mm});
            skCircle(sketch, "E413", {"center": v(153.58, -54.44) * mm, "radius": 2.2 * mm});
            skLineSegment(sketch, "E414", {"start": v(-159.97, 24.75) * mm, "end": v(-159.97, 29.14) * mm});
            skLineSegment(sketch, "E415", {"start": v(-159.97, 9.38) * mm, "end": v(-159.97, 13.77) * mm});
            skLineSegment(sketch, "E416", {"start": v(-160.53, -4.52) * mm, "end": v(-160.53, -0.13) * mm});
            skLineSegment(sketch, "E417", {"start": v(-160.53, -19.9) * mm, "end": v(-160.53, -15.5) * mm});
            skLineSegment(sketch, "E418", {"start": v(160.02, -19.9) * mm, "end": v(160.02, -15.5) * mm});
            skLineSegment(sketch, "E419", {"start": v(160.02, -4.52) * mm, "end": v(160.02, -0.13) * mm});
            skLineSegment(sketch, "E420", {"start": v(160.57, 9.38) * mm, "end": v(160.57, 13.77) * mm});
            skLineSegment(sketch, "E421", {"start": v(160.57, 24.75) * mm, "end": v(160.57, 29.14) * mm});
            skSolve(sketch);
        }
        {
            var Q0;
            Q0 = qSketchRegion(id + "F0", true);
            extrude(context, id + "F1", {"entities" : qUnion([Q0]), "depth" : 101.6 * mm});
        }
        {
            var Q0;
            Q0=makeQuery(id+"F0.imprint","IMPRINT",FACE,{"disambiguationData":[TD([[makeQuery(id+"F0.imprint","IMPRINT",EDGE,{"derivedFrom":sQuery(id+"F0.wireOp",EDGE,"E5.bottom")}),-1.0]])]});
            var Q1;
            {var subQ1=sQuery(id+"F0.wireOp",EDGE,"E58.left");Q1=makeQuery(id+"F0.imprint","IMPRINT",FACE,{"disambiguationData":[TD([[makeQuery(id+"F0.imprint","IMPRINT",EDGE,{"derivedFrom":subQ1}),1.0]])]});}
            var Q2;
            Q2=makeQuery(id+"F0.imprint","IMPRINT",FACE,{"disambiguationData":[TD([[makeQuery(id+"F0.imprint","IMPRINT",EDGE,{"derivedFrom":sQuery(id+"F0.wireOp",EDGE,"E107.bottom")}),-1.0]])]});
            var Q3;
            Q3=makeQuery(id+"F0.imprint","IMPRINT",FACE,{"disambiguationData":[TD([[makeQuery(id+"F0.imprint","IMPRINT",EDGE,{"derivedFrom":sQuery(id+"F0.wireOp",EDGE,"E160.top")}),1.0]])]});
            var Q4;
            Q4=makeQuery(id+"F0.imprint","IMPRINT",FACE,{"disambiguationData":[TD([[makeQuery(id+"F0.imprint","IMPRINT",EDGE,{"derivedFrom":sQuery(id+"F0.wireOp",EDGE,"E209.bottom")}),-1.0]])]});
            var Q5;
            Q5=makeQuery(id+"F0.imprint","IMPRINT",FACE,{"disambiguationData":[TD([[makeQuery(id+"F0.imprint","IMPRINT",EDGE,{"derivedFrom":sQuery(id+"F0.wireOp",EDGE,"E262.top")}),1.0]])]});
            var Q6;
            Q6=makeQuery(id+"F0.imprint","IMPRINT",FACE,{"disambiguationData":[TD([[makeQuery(id+"F0.imprint","IMPRINT",EDGE,{"derivedFrom":sQuery(id+"F0.wireOp",EDGE,"E312.bottom")}),-1.0]])]});
            var Q7;
            {var subQ1=sQuery(id+"F0.wireOp",EDGE,"E365.left");Q7=makeQuery(id+"F0.imprint","IMPRINT",FACE,{"disambiguationData":[TD([[makeQuery(id+"F0.imprint","IMPRINT",EDGE,{"derivedFrom":subQ1}),1.0]])]});}
            extrude(context, id + "F2", {"entities" : qUnion([Q0, Q1, Q2, Q3, Q4, Q5, Q6, Q7]), "operationType" : NewBodyOperationType.ADD, "depth" : 101.6 * mm});
        }
    });
